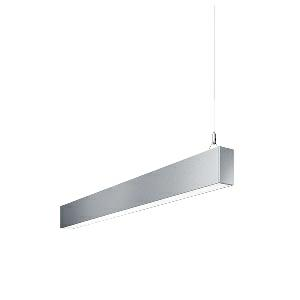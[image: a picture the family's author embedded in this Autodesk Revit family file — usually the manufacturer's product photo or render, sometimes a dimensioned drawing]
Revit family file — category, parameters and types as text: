
# Revit family: idoo_line_-_ilp_3000_840_d_end_00805693_1dd9
name_source: partatom
category: Lighting Fixtures
units: mm (PartAtom-declared; Revit-internal decimal feet)

## family parameters
Cut with Voids When Loaded = No
Host = Face
Light Source = No
Part Type = Normal
Room Calculation Point = No
Round Connector Dimension = Use Diameter
Shared = No

## types (1)
- IDOO.line - ILP 3000/840/D END (1 x LED, 3150 lm, 4000K)
    Apparent Load = 23 VA
    Approval mark = CE
    CIE Flux Codes = 66 91 98 40 100
    Color Rendering = 80-89
    Color Temperature = 4000K
    Control Gear = Electronic ballast
    Default Elevation = 1800 mm
    Description = ILP 3000/840/D|Suspended luminaire|light source: LED|connected load: 220-240 V, 50/60 Hz|Power consumption: approx. 23 W|standby: approx. 0,20|luminous flux: 3150 lm|luminous efficacy: 136 lm/W|light distribution: Direct/indirect|direct ratio: approx. 40 %|colour temperature: Cold white, ca. 4000 K|color rendering index (CRI): >= 80|chromaticity tolerance:  3 SDCM|System of protection: IP 40|technology: Continuously dimmable|luminaire body|material: Sectional aluminium|colour: Silver|lamp cover: Acrylic (PMMA), Clear|mains lead: 1,0 m With free stranded wires|Fastening: Steel cable 0.3 - 0.7 m|glare control: Prism aperture|luminance(L65): <= 2700 cd/m|unified glare rating(4H 8H): <=  16|special features: DALI Load 1x, TouchDIM - dimming via standard switch, Through-wired, up to 18 m on one mains connection, Flicker-free, Suitable as emergency lighting, Mechanical and electrical connection of the individual modules without tools|
    Frequency = 50 Hz
    Height = 110 mm
    Lamp = 1 x LED
    Lamp Light Flux = 3150 lm
    Lamp count = 1
    Length = 1128 mm
    Luminous efficacy = 137 lm/W
    Manufacturer = Waldmann
    ModVariant = No
    Model = 00805693
    Mounting Place = Ceiling
    Mounting Type = Pendant
    Number of Poles = 1
    OnlyDefault = Yes
    Power Factor = 1
    Product Name = IDOO.line - ILP 3000/840/D END
    Product group = Suspended luminaire
    ProductGroupID = 9
    Protection Class = Protection class I
    Protection Degree = IP 40
    RLX_Detail_Level = 1
    RLX_Emergency_Light_Flux = 0 lm
    RLX_Emergency_Type = 0
    RLX_Emergency_Type_DB = No
    RlxData = <blob elided: 19829 chars, md5=d02e230f>
    Socket = socket
    Standby Power = 0 W
    System Light Flux = 3150 lm
    System Power = 23 W
    Type Comments = Product without accessories
    Type Image = 113306000-00692582.jpg
    URL = http://relux.com
    VarID = ---
    Voltage = 230 V
    Voltage Range = 220-240 V
    Weight = 0.00 kg
    Width = 60 mm  [stored 0.19685 ft]

note: [stored X ft] marks values corroborated as IEEE doubles in the binary element streams (Revit-internal decimal feet)

## geometry (parser evidence)
native form markers: Blend x4, Sweep x14
no freeform markers — native parametric forms only
